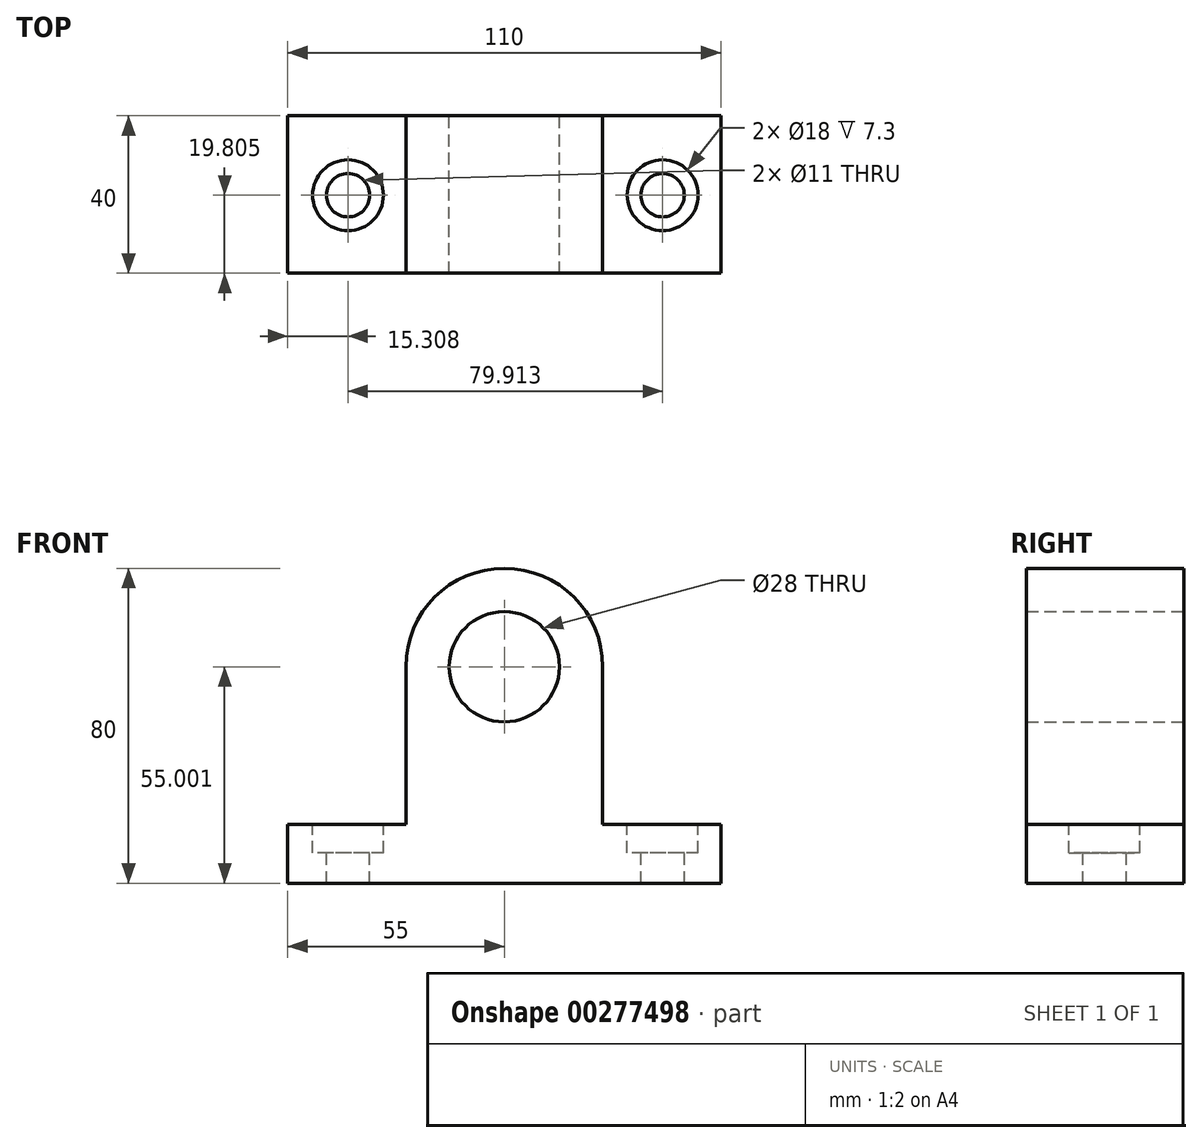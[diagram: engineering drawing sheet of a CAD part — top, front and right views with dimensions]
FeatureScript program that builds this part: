
annotation { "Feature Type Name" : "Feature", "Feature Type Description" : "" }
export const myFeature = defineFeature(function(context is Context, id is Id, definition is map)
    precondition{}
    {
        {
            var Q0;
            Q0=qCreatedBy(makeId("Front.planeOp"),FACE);
            var sketch = newSketch(context, id + "F0", { "sketchPlane" : qUnion([Q0])});
            skLineSegment(sketch, "E0", {"start": v(0, -27.27) * mm, "end": v(55, -27.27) * mm});
            skLineSegment(sketch, "E1", {"start": v(55, -27.27) * mm, "end": v(55, -12.27) * mm});
            skLineSegment(sketch, "E2", {"start": v(55, -12.27) * mm, "end": v(25, -12.27) * mm});
            skLineSegment(sketch, "E3", {"start": v(25, -12.27) * mm, "end": v(25, 27.73) * mm});
            skLineSegment(sketch, "E4", {"start": v(0, -27.27) * mm, "end": v(-55, -27.27) * mm});
            skLineSegment(sketch, "E5", {"start": v(-55, -27.27) * mm, "end": v(-55, -12.27) * mm});
            skLineSegment(sketch, "E6", {"start": v(-55, -12.27) * mm, "end": v(-25, -12.27) * mm});
            skLineSegment(sketch, "E7", {"start": v(-25, -12.27) * mm, "end": v(-25, 27.73) * mm});
            skArc(sketch, "E8", {"start": v(-25, 27.73) * mm, "mid": v(0, 52.73) * mm, "end": v(25, 27.73) * mm});
            skCircle(sketch, "E9", {"center": v(0, 27.73) * mm, "radius": 14 * mm});
            skSolve(sketch);
        }
        {
            var Q0;
            Q0=makeQuery(id+"F0.imprint","IMPRINT",FACE,{"disambiguationData":[TD([[makeQuery(id+"F0.imprint","IMPRINT",EDGE,{"derivedFrom":sQuery(id+"F0.wireOp",EDGE,"E0")}),1.0]])]});
            extrude(context, id + "F1", {"entities" : qUnion([Q0]), "depth" : 40 * mm});
        }
        {
            var Q0;
            Q0=makeQuery(id+"F1.opExtrude","SWEPT_FACE",FACE,{"disambiguationData":[OSD([sQuery(id+"F0.wireOp",EDGE,"E2")])]});
            var sketch = newSketch(context, id + "F2", { "sketchPlane" : qUnion([Q0])});
            skCircle(sketch, "E10", {"center": v(40.22, -20.2) * mm, "radius": 9 * mm});
            skCircle(sketch, "E11", {"center": v(40.22, -20.2) * mm, "radius": 5.5 * mm});
            skCircle(sketch, "E12", {"center": v(-39.7, -20.2) * mm, "radius": 9 * mm});
            skCircle(sketch, "E13", {"center": v(-39.7, -20.2) * mm, "radius": 5.5 * mm});
            skSolve(sketch);
        }
        {
            var Q0;
            Q0 = qSketchRegion(id + "F2", true);
            extrude(context, id + "F3", {"entities" : qUnion([Q0]), "operationType" : NewBodyOperationType.REMOVE, "oppositeDirection" : true, "depth" : 7.3 * mm});
        }
        {
            var Q0;
            Q0=makeQuery(id+"F3.boolean.opBoolean","SPLIT",FACE,{"disambiguationData":[TD([makeQuery(id+"F3.opExtrude","SWEPT_FACE",FACE,{"disambiguationData":[OSD([sQuery(id+"F2.wireOp",EDGE,"E13")])]})])],"derivedFrom":makeQuery(id+"F1.opExtrude","SWEPT_FACE",FACE,{"disambiguationData":[OSD([sQuery(id+"F0.wireOp",EDGE,"E6")])]})});
            var Q1;
            Q1=makeQuery(id+"F3.boolean.opBoolean","SPLIT",FACE,{"disambiguationData":[TD([makeQuery(id+"F3.opExtrude","SWEPT_FACE",FACE,{"disambiguationData":[OSD([sQuery(id+"F2.wireOp",EDGE,"E11")])]})])],"derivedFrom":makeQuery(id+"F1.opExtrude","SWEPT_FACE",FACE,{"disambiguationData":[OSD([sQuery(id+"F0.wireOp",EDGE,"E2")])]})});
            extrude(context, id + "F4", {"entities" : qUnion([Q0, Q1]), "operationType" : NewBodyOperationType.REMOVE, "oppositeDirection" : true, "depth" : 15 * mm});
        }
    });
